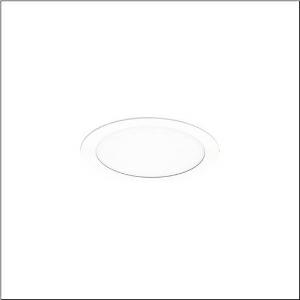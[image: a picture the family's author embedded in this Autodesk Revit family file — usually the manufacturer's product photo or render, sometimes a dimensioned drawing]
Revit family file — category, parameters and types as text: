
# Revit family: lunis_21_l_51db16td91c
name_source: partatom
category: Lighting Fixtures
units: mm (PartAtom-declared; Revit-internal decimal feet)

## family parameters
Cut with Voids When Loaded = No
Host = Face
Light Source = No
Part Type = Normal
Room Calculation Point = No
Round Connector Dimension = Use Diameter
Shared = No

## types (1)
- --- (1 x LED 3000 K ... 6500 K, 3290 lm, 25.4 W, 4000K)
    Apparent Load = 25 VA
    CIE Flux Codes = 50 80 96 100 100
    Color Rendering = 80
    Color Temperature = 4000K
    Default Elevation = 1800 mm
    Description = Lunis 21 L, downlight, light control with lens, of PMMA, optical cover: cover panel, of PC, opal, light emission: direct distribution, LED rated luminous flux: 3.290lm, light colour: 8tw, with terminal, 5-pole, mains connection: 220..240V, AC/DC, 0/50..60Hz, housing, round, of diecast aluminium, traffic white (RAL 9016), diameter: 165mm, clamping range: 1..40mm, protection rating (complete): IP20, protection rating (on room side): IP54, insulation class (complete): insulation class II (safety insulation), certification: CE, impact resistance: IK03, packaging unit: 1 piece
    Height = 0 mm  [stored 0 ft]
    Lamp = 1 x LED 3000 K ... 6500 K
    Lamp Light Flux = 3290 lm
    Lamp Power = 25.4 W
    Lamp count = 1
    Length = 165 mm
    Luminous efficacy = 130 lm/W
    Manufacturer = Siteco
    ModVariant = No
    Model = 51DB16TD91C
    Mounting Place = Ceiling
    Mounting Type = Recessed
    Number of Poles = 1
    OnlyDefault = Yes
    Power Factor = 1
    Product Name = Lunis 21 L
    Product group = downlight
    ProductGroupID = 401
    Protection Class = Protection class II
    Protection Degree = IP 20
    RLX_Detail_Level = 1
    RLX_Emergency_Light_Flux = 0 lm
    RLX_Emergency_Type = 0
    RLX_Emergency_Type_DB = No
    RlxData = <blob elided: 12429 chars, md5=6b8231ad>
    Socket = socket
    Standby Power = 0 W
    System Light Flux = 3290 lm
    System Power = 25 W
    Type Comments = individual setting: CCT=4000K, colour temperature 4000K, luminous flux: 100 % | (ON | ON | OFF | OFF) | 700 mA
    Type Image = l_1291165.jpg
    URL = http://relux.com
    VarID = @adj_036611
    Voltage = 0 V
    Weight = 0.00 kg
    Width = 0 mm  [stored 0 ft]

note: [stored X ft] marks values corroborated as IEEE doubles in the binary element streams (Revit-internal decimal feet)

## geometry (parser evidence)
native form markers: Sweep x8
no freeform markers — native parametric forms only
